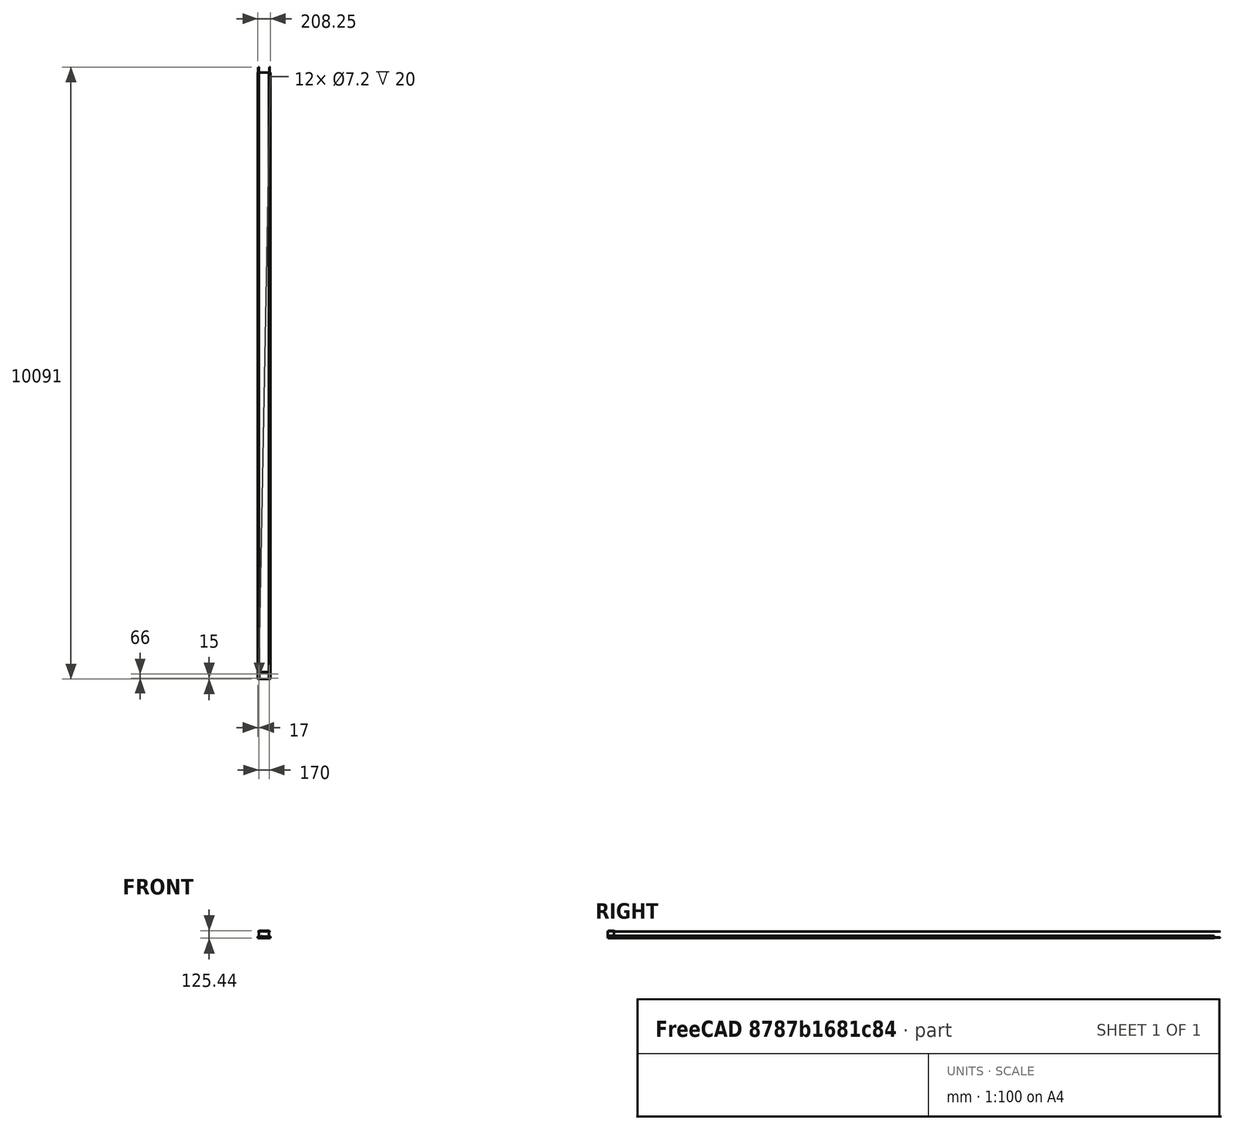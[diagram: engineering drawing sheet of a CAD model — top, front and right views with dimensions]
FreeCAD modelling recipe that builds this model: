
FCSTD DOCUMENT  (FreeCAD 0.15R4671 (Git))
Label: EBOX_Top
License: All rights reserved
LicenseURL: http://en.wikipedia.org/wiki/All_rights_reserved
objects: Sketcher::SketchObject×14, PartDesign::Pocket×9, Part::Feature×5, Mesh::Feature×5, PartDesign::Pad×5, PartDesign::Fillet×5
note: 52 computed .brp shape members not serialized (recipe doc carries the construction recipe); baked Part::Feature solids carry a one-line shape summary decoded from their .brp

FEATURE [Part::Feature] Part__Feature003  label="MKS_Gen_V1p3"
  Placement = pos=(4,-58,9) rot=(0,0,1;0rad)
  shape: bbox 143.1 x 84.2 x 22.31 mm, 8746 faces, 0 solids (baked)
FEATURE [Part::Feature] Part__Feature  label="OB1515_180mm"
  Placement = pos=(-90,0,0) rot=(0,1,0;1.5708rad)
  shape: bbox 180 x 15 x 15 mm, 158 faces (baked)
FEATURE [Part::Feature] Part__Feature004  label="OB1515_180mm001"
  Placement = pos=(-90,0,100) rot=(0,1,0;1.5708rad)
  shape: bbox 180 x 15 x 15 mm, 158 faces (baked)
FEATURE [Mesh::Feature] _0mmFan  label="40mmFan"
  Placement = pos=(15,-41,56) rot=(0,0,1;0rad)
FEATURE [Sketcher::SketchObject] Sketch
  Placement = pos=(0,0,-7.5) rot=(0,0,1;0rad)
  sketch-geometry (4):
    g0: LineSegment StartX=82 StartY=-8 StartZ=0 EndX=-82 EndY=-8 EndZ=0
    g1: LineSegment StartX=-82 StartY=-8 StartZ=0 EndX=-82 EndY=-106 EndZ=0
    g2: LineSegment StartX=-82 StartY=-106 StartZ=0 EndX=82 EndY=-106 EndZ=0
    g3: LineSegment StartX=82 StartY=-106 StartZ=0 EndX=82 EndY=-8 EndZ=0
  constraints (8):
    c: Coincident(g0,g1)
    c: Coincident(g1,g2)
    c: Coincident(g2,g3)
    c: Coincident(g3,g0)
    c: Horizontal(g0)
    c: Horizontal(g2)
    c: Vertical(g1)
    c: Vertical(g3)
FEATURE [PartDesign::Pad] Pad
  Length = 115
  Length2 = 100
  Placement = pos=(0,0,-7.5) rot=(0,0,1;0rad)
  Sketch = -> Sketch
  Type = 0
FEATURE [Sketcher::SketchObject] Sketch001
  Placement = pos=(0,0,107.5) rot=(0,0,1;0rad)
  Support = -> Pad [Face6]
  sketch-geometry (4):
    g0: LineSegment StartX=-79 StartY=-11 StartZ=0 EndX=79 EndY=-11 EndZ=0
    g1: LineSegment StartX=79 StartY=-11 StartZ=0 EndX=79 EndY=-103 EndZ=0
    g2: LineSegment StartX=79 StartY=-103 StartZ=0 EndX=-79 EndY=-103 EndZ=0
    g3: LineSegment StartX=-79 StartY=-103 StartZ=0 EndX=-79 EndY=-11 EndZ=0
  constraints (8):
    c: Coincident(g0,g1)
    c: Coincident(g1,g2)
    c: Coincident(g2,g3)
    c: Coincident(g3,g0)
    c: Horizontal(g0)
    c: Horizontal(g2)
    c: Vertical(g1)
    c: Vertical(g3)
FEATURE [PartDesign::Pocket] Pocket
  Length = 112
  Placement = pos=(0,0,-7.5) rot=(0,0,1;0rad)
  Sketch = -> Sketch001
  Type = 0
FEATURE [Sketcher::SketchObject] Sketch002
  Placement = pos=(0,0,-4.5) rot=(0,0,1;0rad)
  Support = -> Pocket [Face11]
  sketch-geometry (4):
    g0: Circle CenterX=71.2811 CenterY=-20.1362 CenterZ=0 NormalX=0 NormalY=0 NormalZ=1 Radius=4
    g1: Circle CenterX=71.2541 CenterY=-95.8403 CenterZ=0 NormalX=0 NormalY=0 NormalZ=1 Radius=4
    g2: Circle CenterX=-63.2692 CenterY=-95.845 CenterZ=0 NormalX=0 NormalY=0 NormalZ=1 Radius=4
    g3: Circle CenterX=-63.279 CenterY=-20.1649 CenterZ=0 NormalX=0 NormalY=0 NormalZ=1 Radius=4
  constraints (4):
    c: Radius(g0) = 4
    c: Equal(g0,g1)
    c: Equal(g0,g2)
    c: Equal(g0,g3)
FEATURE [PartDesign::Pad] Pad001
  Length = 13.5
  Length2 = 100
  Placement = pos=(0,0,-7.5) rot=(0,0,1;0rad)
  Sketch = -> Sketch002
  Type = 0
FEATURE [Sketcher::SketchObject] Sketch003
  Placement = pos=(0,0,9) rot=(0,0,1;0rad)
  Support = -> Pad001 [Face17]
  sketch-geometry (4):
    g0: Circle CenterX=-63.2989 CenterY=-20.1665 CenterZ=0 NormalX=0 NormalY=0 NormalZ=1 Radius=1.5
    g1: Circle CenterX=71.3054 CenterY=-20.1275 CenterZ=0 NormalX=0 NormalY=0 NormalZ=1 Radius=1.5
    g2: Circle CenterX=71.282 CenterY=-95.8363 CenterZ=0 NormalX=0 NormalY=0 NormalZ=1 Radius=1.5
    g3: Circle CenterX=-63.2831 CenterY=-95.8609 CenterZ=0 NormalX=0 NormalY=0 NormalZ=1 Radius=1.5
  constraints (4):
    c: Radius(g0) = 1.5
    c: Equal(g0,g1)
    c: Equal(g0,g2)
    c: Equal(g0,g3)
FEATURE [PartDesign::Pocket] Pocket001
  Length = 8
  Placement = pos=(0,0,-7.5) rot=(0,0,1;0rad)
  Sketch = -> Sketch003
  Type = 0
FEATURE [Sketcher::SketchObject] Sketch004
  Placement = pos=(0,0,107.5) rot=(0,0,1;0rad)
  Support = -> Pocket001 [Face5]
  sketch-geometry (4):
    g0: LineSegment StartX=-82 StartY=-106 StartZ=0 EndX=82 EndY=-106 EndZ=0
    g1: LineSegment StartX=82 StartY=-106 StartZ=0 EndX=82 EndY=-8 EndZ=0
    g2: LineSegment StartX=82 StartY=-8 StartZ=0 EndX=-82 EndY=-8 EndZ=0
    g3: LineSegment StartX=-82 StartY=-8 StartZ=0 EndX=-82 EndY=-106 EndZ=0
  constraints (8):
    c: Coincident(g0,g1)
    c: Coincident(g1,g2)
    c: Coincident(g2,g3)
    c: Coincident(g3,g0)
    c: Horizontal(g0)
    c: Horizontal(g2)
    c: Vertical(g1)
    c: Vertical(g3)
FEATURE [PartDesign::Pad] Pad002
  Length = 3
  Length2 = 100
  Placement = pos=(0,0,-7.5) rot=(0,0,1;0rad)
  Reversed = true
  Sketch = -> Sketch004
  Type = 0
FEATURE [Part::Feature] Pad002001  label="Pad003"
  shape: bbox 164 x 98 x 115 mm, 28 faces (baked)
FEATURE [Sketcher::SketchObject] Sketch005
  Placement = pos=(0,0,-7.5) rot=(1,0,0;3.14159rad)
  Support = -> Pad002001 [Face1]
  sketch-geometry (16):
    g0: ArcOfCircle CenterX=84 CenterY=25 CenterZ=0 NormalX=0 NormalY=0 NormalZ=1 Radius=7 StartAngle=4.71239 EndAngle=7.85398
    g1: ArcOfCircle CenterX=84 CenterY=91 CenterZ=0 NormalX=0 NormalY=0 NormalZ=1 Radius=7 StartAngle=4.71239 EndAngle=7.85398
    g2: ArcOfCircle CenterX=-84 CenterY=91 CenterZ=0 NormalX=0 NormalY=0 NormalZ=1 Radius=7 StartAngle=1.5708 EndAngle=4.71239
    g3: ArcOfCircle CenterX=-84 CenterY=25 CenterZ=0 NormalX=0 NormalY=0 NormalZ=1 Radius=7 StartAngle=1.5708 EndAngle=4.71239
    g4: LineSegment StartX=-84 StartY=32 StartZ=0 EndX=-81 EndY=32 EndZ=0
    g5: LineSegment StartX=-81 StartY=32 StartZ=0 EndX=-81 EndY=18 EndZ=0
    g6: LineSegment StartX=-81 StartY=18 StartZ=0 EndX=-84 EndY=18 EndZ=0
    g7: LineSegment StartX=-84 StartY=98 StartZ=0 EndX=-81 EndY=98 EndZ=0
    g8: LineSegment StartX=-81 StartY=98 StartZ=0 EndX=-81 EndY=84 EndZ=0
    g9: LineSegment StartX=-81 StartY=84 StartZ=0 EndX=-84 EndY=84 EndZ=0
    g10: LineSegment StartX=84 StartY=98 StartZ=0 EndX=81 EndY=98 EndZ=0
    g11: LineSegment StartX=81 StartY=98 StartZ=0 EndX=81 EndY=84 EndZ=0
    g12: LineSegment StartX=81 StartY=84 StartZ=0 EndX=84 EndY=84 EndZ=0
    g13: LineSegment StartX=84 StartY=32 StartZ=0 EndX=81 EndY=32 EndZ=0
    g14: LineSegment StartX=81 StartY=32 StartZ=0 EndX=81 EndY=18 EndZ=0
    g15: LineSegment StartX=81 StartY=18 StartZ=0 EndX=84 EndY=18 EndZ=0
  constraints (25):
    c: Tangent(g3,g4) = 1.5708
    c: Coincident(g4,g5)
    c: Vertical(g5)
    c: Coincident(g5,g6)
    c: Coincident(g6,g3)
    c: Horizontal(g6)
    c: Tangent(g6,g3)
    c: Tangent(g2,g7) = 1.5708
    c: Coincident(g7,g8)
    c: Vertical(g8)
    c: Coincident(g8,g9)
    c: Coincident(g9,g2)
    c: Horizontal(g9)
    c: Tangent(g1,g10) = -1.5708
    c: Coincident(g10,g11)
    c: Vertical(g11)
    c: Coincident(g11,g12)
    c: Coincident(g12,g1)
    c: Horizontal(g12)
    c: Tangent(g0,g13) = -1.5708
    c: Coincident(g13,g14)
    c: Vertical(g14)
    c: Coincident(g14,g15)
    c: Coincident(g15,g0)
    c: Horizontal(g15)
FEATURE [PartDesign::Pad] Pad002002
  Length = 35
  Length2 = 100
  Reversed = true
  Sketch = -> Sketch005
  Type = 0
FEATURE [PartDesign::Fillet] Fillet
  Base = -> Pad002002 [Edge28,Edge26,Edge22,Edge24,Edge8,Edge12,Edge14,Edge10]
  Radius = 1.99
FEATURE [Sketcher::SketchObject] Sketch006
  Placement = pos=(0,-106,0) rot=(1,0,0;1.5708rad)
  Support = -> Fillet [Face7]
  sketch-geometry (10):
    g0: LineSegment StartX=-82 StartY=29 StartZ=0 EndX=-82 EndY=27 EndZ=0
    g1: LineSegment StartX=-82 StartY=27 StartZ=0 EndX=-91 EndY=18 EndZ=0
    g2: LineSegment StartX=-91 StartY=18 StartZ=0 EndX=-92 EndY=18 EndZ=0
    g3: LineSegment StartX=-92 StartY=18 StartZ=0 EndX=-92 EndY=29 EndZ=0
    g4: LineSegment StartX=-92 StartY=29 StartZ=0 EndX=-82 EndY=29 EndZ=0
    g5: LineSegment StartX=82 StartY=29 StartZ=0 EndX=82 EndY=27 EndZ=0
    g6: LineSegment StartX=82 StartY=27 StartZ=0 EndX=91 EndY=18 EndZ=0
    g7: LineSegment StartX=91 StartY=18 StartZ=0 EndX=92 EndY=18 EndZ=0
    g8: LineSegment StartX=92 StartY=18 StartZ=0 EndX=92 EndY=29 EndZ=0
    g9: LineSegment StartX=92 StartY=29 StartZ=0 EndX=82 EndY=29 EndZ=0
  constraints (18):
    c: Vertical(g0)
    c: Coincident(g0,g1)
    c: Coincident(g1,g2)
    c: Horizontal(g2)
    c: Coincident(g2,g3)
    c: Vertical(g3)
    c: Coincident(g3,g4)
    c: Coincident(g4,g0)
    c: Horizontal(g4)
    c: Vertical(g5)
    c: Coincident(g5,g6)
    c: Coincident(g6,g7)
    c: Horizontal(g7)
    c: Coincident(g7,g8)
    c: Vertical(g8)
    c: Coincident(g8,g9)
    c: Coincident(g9,g5)
    c: Horizontal(g9)
FEATURE [PartDesign::Pocket] Pocket002
  Length = 5
  Sketch = -> Sketch006
  Type = 1
FEATURE [Mesh::Feature] HexNutStyle1_M3
  Placement = pos=(86.28,1.15,-100) rot=(0,0,1;0.523599rad)
FEATURE [Mesh::Feature] HexNutStyle1_M
  Placement = pos=(86.28,-64.85,-100) rot=(0,0,1;0.523599rad)
FEATURE [Mesh::Feature] HexNutStyle1_M004
  Placement = pos=(-83.72,1.15,-100) rot=(0,0,1;0.523599rad)
FEATURE [Mesh::Feature] HexNutStyle1_M005
  Placement = pos=(-83.72,-64.85,-100) rot=(0,0,1;0.523599rad)
FEATURE [Sketcher::SketchObject] Sketch007
  Placement = pos=(0,0,-7.5) rot=(1,0,0;3.14159rad)
  Support = -> Pocket002 [Face2]
  sketch-geometry (4):
    g0: Circle CenterX=-85 CenterY=91 CenterZ=0 NormalX=0 NormalY=0 NormalZ=1 Radius=1.8
    g1: Circle CenterX=-85 CenterY=25 CenterZ=0 NormalX=0 NormalY=0 NormalZ=1 Radius=1.8
    g2: Circle CenterX=85 CenterY=25 CenterZ=0 NormalX=0 NormalY=0 NormalZ=1 Radius=1.8
    g3: Circle CenterX=85 CenterY=91 CenterZ=0 NormalX=0 NormalY=0 NormalZ=1 Radius=1.8
  constraints (4):
    c: Radius(g0) = 1.8
    c: Equal(g0,g1)
    c: Equal(g0,g2)
    c: Equal(g0,g3)
FEATURE [PartDesign::Pocket] Pocket003
  Length = 28
  Sketch = -> Sketch007
  Type = 0
FEATURE [Sketcher::SketchObject] Sketch008
  Placement = pos=(0,0,-7.5) rot=(1,0,0;3.14159rad)
  Support = -> Pocket003 [Face2]
  sketch-geometry (4):
    g0: Circle CenterX=85 CenterY=91 CenterZ=0 NormalX=0 NormalY=0 NormalZ=1 Radius=3.6
    g1: Circle CenterX=85 CenterY=25 CenterZ=0 NormalX=0 NormalY=0 NormalZ=1 Radius=3.6
    g2: Circle CenterX=-85 CenterY=91 CenterZ=0 NormalX=0 NormalY=0 NormalZ=1 Radius=3.6
    g3: Circle CenterX=-85 CenterY=25 CenterZ=0 NormalX=0 NormalY=0 NormalZ=1 Radius=3.6
  constraints (4):
    c: Radius(g0) = 3.6
    c: Equal(g0,g1)
    c: Equal(g0,g2)
    c: Equal(g0,g3)
FEATURE [PartDesign::Pocket] Pocket004
  Length = 20
  Sketch = -> Sketch008
  Type = 0
FEATURE [Sketcher::SketchObject] Sketch009
  Placement = pos=(0,-8,0) rot=(0,0.707107,0.707107;3.14159rad)
  Support = -> Pocket004 [Face1]
  sketch-geometry (16):
    g0: LineSegment StartX=-81 StartY=7.5 StartZ=0 EndX=-101 EndY=7.5 EndZ=0
    g1: LineSegment StartX=-101 StartY=7.5 StartZ=0 EndX=-101 EndY=-7.5 EndZ=0
    g2: LineSegment StartX=-101 StartY=-7.5 StartZ=0 EndX=-81 EndY=-7.5 EndZ=0
    g3: LineSegment StartX=-81 StartY=-7.5 StartZ=0 EndX=-81 EndY=7.5 EndZ=0
    g4: LineSegment StartX=81 StartY=7.5 StartZ=0 EndX=101 EndY=7.5 EndZ=0
    g5: LineSegment StartX=101 StartY=7.5 StartZ=0 EndX=101 EndY=-7.5 EndZ=0
    g6: LineSegment StartX=101 StartY=-7.5 StartZ=0 EndX=81 EndY=-7.5 EndZ=0
    g7: LineSegment StartX=81 StartY=-7.5 StartZ=0 EndX=81 EndY=7.5 EndZ=0
    g8: LineSegment StartX=-92 StartY=107.5 StartZ=0 EndX=-81 EndY=107.5 EndZ=0
    g9: LineSegment StartX=-81 StartY=107.5 StartZ=0 EndX=-81 EndY=92.5 EndZ=0
    g10: LineSegment StartX=-81 StartY=92.5 StartZ=0 EndX=-92 EndY=92.5 EndZ=0
    g11: LineSegment StartX=-92 StartY=92.5 StartZ=0 EndX=-92 EndY=107.5 EndZ=0
    g12: LineSegment StartX=81 StartY=92.5 StartZ=0 EndX=92 EndY=92.5 EndZ=0
    g13: LineSegment StartX=92 StartY=92.5 StartZ=0 EndX=92 EndY=107.5 EndZ=0
    g14: LineSegment StartX=92 StartY=107.5 StartZ=0 EndX=81 EndY=107.5 EndZ=0
    g15: LineSegment StartX=81 StartY=107.5 StartZ=0 EndX=81 EndY=92.5 EndZ=0
  constraints (32):
    c: Coincident(g0,g1)
    c: Coincident(g1,g2)
    c: Coincident(g2,g3)
    c: Coincident(g3,g0)
    c: Horizontal(g0)
    c: Horizontal(g2)
    c: Vertical(g1)
    c: Vertical(g3)
    c: Coincident(g4,g5)
    c: Coincident(g5,g6)
    c: Coincident(g6,g7)
    c: Coincident(g7,g4)
    c: Horizontal(g4)
    c: Horizontal(g6)
    c: Vertical(g5)
    c: Vertical(g7)
    c: Coincident(g8,g9)
    c: Coincident(g9,g10)
    c: Coincident(g10,g11)
    c: Coincident(g11,g8)
    c: Horizontal(g8)
    c: Horizontal(g10)
    c: Vertical(g9)
    c: Vertical(g11)
    c: Coincident(g12,g13)
    c: Coincident(g13,g14)
    c: Coincident(g14,g15)
    c: Coincident(g15,g12)
    c: Horizontal(g12)
    c: Horizontal(g14)
    c: Vertical(g13)
    c: Vertical(g15)
FEATURE [PartDesign::Pad] Pad002003
  Length = 7
  Length2 = 100
  Reversed = true
  Sketch = -> Sketch009
  Type = 0
FEATURE [PartDesign::Fillet] Fillet001
  Base = -> Pad002003 [Edge22,Edge63]
  Radius = 4
FEATURE [PartDesign::Fillet] Fillet002
  Base = -> Fillet001 [Edge111,Edge77,Edge88,Edge51,Edge112,Edge78,Edge128,Edge92]
  Radius = 4
FEATURE [PartDesign::Fillet] Fillet003
  Base = -> Fillet002 [Edge120,Edge46]
  Radius = 4
FEATURE [Sketcher::SketchObject] Sketch010
  Placement = pos=(0,-15,0) rot=(1,0,0;1.5708rad)
  Support = -> Fillet003 [Face35]
  sketch-geometry (4):
    g0: Circle CenterX=-87.5 CenterY=100 CenterZ=0 NormalX=0 NormalY=0 NormalZ=1 Radius=1.8
    g1: Circle CenterX=87.5 CenterY=100 CenterZ=0 NormalX=0 NormalY=0 NormalZ=1 Radius=1.8
    g2: Circle CenterX=95 CenterY=0 CenterZ=0 NormalX=0 NormalY=0 NormalZ=1 Radius=1.8
    g3: Circle CenterX=-95 CenterY=0 CenterZ=0 NormalX=0 NormalY=0 NormalZ=1 Radius=1.8
  constraints (6):
    c: PointOnObject(g2,g-1)
    c: PointOnObject(g3,g-1)
    c: Radius(g0) = 1.8
    c: Equal(g0,g1)
    c: Equal(g0,g2)
    c: Equal(g0,g3)
FEATURE [PartDesign::Pocket] Pocket005
  Length = 5
  Sketch = -> Sketch010
  Type = 1
FEATURE [Sketcher::SketchObject] Sketch011
  Placement = pos=(0,-15,0) rot=(1,0,0;1.5708rad)
  Support = -> Pocket005 [Face31]
  sketch-geometry (4):
    g0: Circle CenterX=-87.5 CenterY=100 CenterZ=0 NormalX=0 NormalY=0 NormalZ=1 Radius=3.5
    g1: Circle CenterX=87.5 CenterY=100 CenterZ=0 NormalX=0 NormalY=0 NormalZ=1 Radius=3.5
    g2: Circle CenterX=95 CenterY=0 CenterZ=0 NormalX=0 NormalY=0 NormalZ=1 Radius=3.5
    g3: Circle CenterX=-95 CenterY=0 CenterZ=0 NormalX=0 NormalY=0 NormalZ=1 Radius=3.5
  constraints (6):
    c: PointOnObject(g2,g-1)
    c: PointOnObject(g3,g-1)
    c: Radius(g0) = 3.5
    c: Equal(g0,g1)
    c: Equal(g0,g2)
    c: Equal(g0,g3)
FEATURE [PartDesign::Pocket] Pocket006
  Length = 3
  Sketch = -> Sketch011
  Type = 0
FEATURE [PartDesign::Fillet] Fillet004
  Base = -> Pocket006 [Edge49,Edge45,Edge78,Edge79,Edge139]
  Radius = 1
FEATURE [Sketcher::SketchObject] Sketch012
  Placement = pos=(0,-106,0) rot=(1,0,0;1.5708rad)
  Support = -> Fillet004 [Face26]
  sketch-geometry (4):
    g0: LineSegment StartX=-46 StartY=21.5 StartZ=0 EndX=-33.5 EndY=21.5 EndZ=0
    g1: LineSegment StartX=-33.5 StartY=21.5 StartZ=0 EndX=-33.5 EndY=10.5 EndZ=0
    g2: LineSegment StartX=-33.5 StartY=10.5 StartZ=0 EndX=-46 EndY=10.5 EndZ=0
    g3: LineSegment StartX=-46 StartY=10.5 StartZ=0 EndX=-46 EndY=21.5 EndZ=0
  constraints (8):
    c: Coincident(g0,g1)
    c: Coincident(g1,g2)
    c: Coincident(g2,g3)
    c: Coincident(g3,g0)
    c: Horizontal(g0)
    c: Horizontal(g2)
    c: Vertical(g1)
    c: Vertical(g3)
FEATURE [PartDesign::Pocket] Pocket007
  Length = 5
  Sketch = -> Sketch012
  Type = 0
FEATURE [Part::Feature] Part__Feature005  label="EBOX_Bottom"
  shape: bbox 202 x 98 x 22 mm, 90 faces (baked)
FEATURE [Sketcher::SketchObject] Sketch013
  Placement = pos=(0,-106,0) rot=(1,0,0;1.5708rad)
  Support = -> Pocket007 [Face22]
  sketch-geometry (4):
    g0: LineSegment StartX=-102 StartY=14.75 StartZ=0 EndX=106.25 EndY=14.75 EndZ=0
    g1: LineSegment StartX=106.25 StartY=14.75 StartZ=0 EndX=106.25 EndY=-10.4399 EndZ=0
    g2: LineSegment StartX=106.25 StartY=-10.4399 StartZ=0 EndX=-102 EndY=-10.4399 EndZ=0
    g3: LineSegment StartX=-102 StartY=-10.4399 StartZ=0 EndX=-102 EndY=14.75 EndZ=0
  constraints (8):
    c: Coincident(g0,g1)
    c: Coincident(g1,g2)
    c: Coincident(g2,g3)
    c: Coincident(g3,g0)
    c: Horizontal(g0)
    c: Horizontal(g2)
    c: Vertical(g1)
    c: Vertical(g3)
FEATURE [PartDesign::Pocket] Pocket008
  Length = 5
  Sketch = -> Sketch013
  Type = 1
